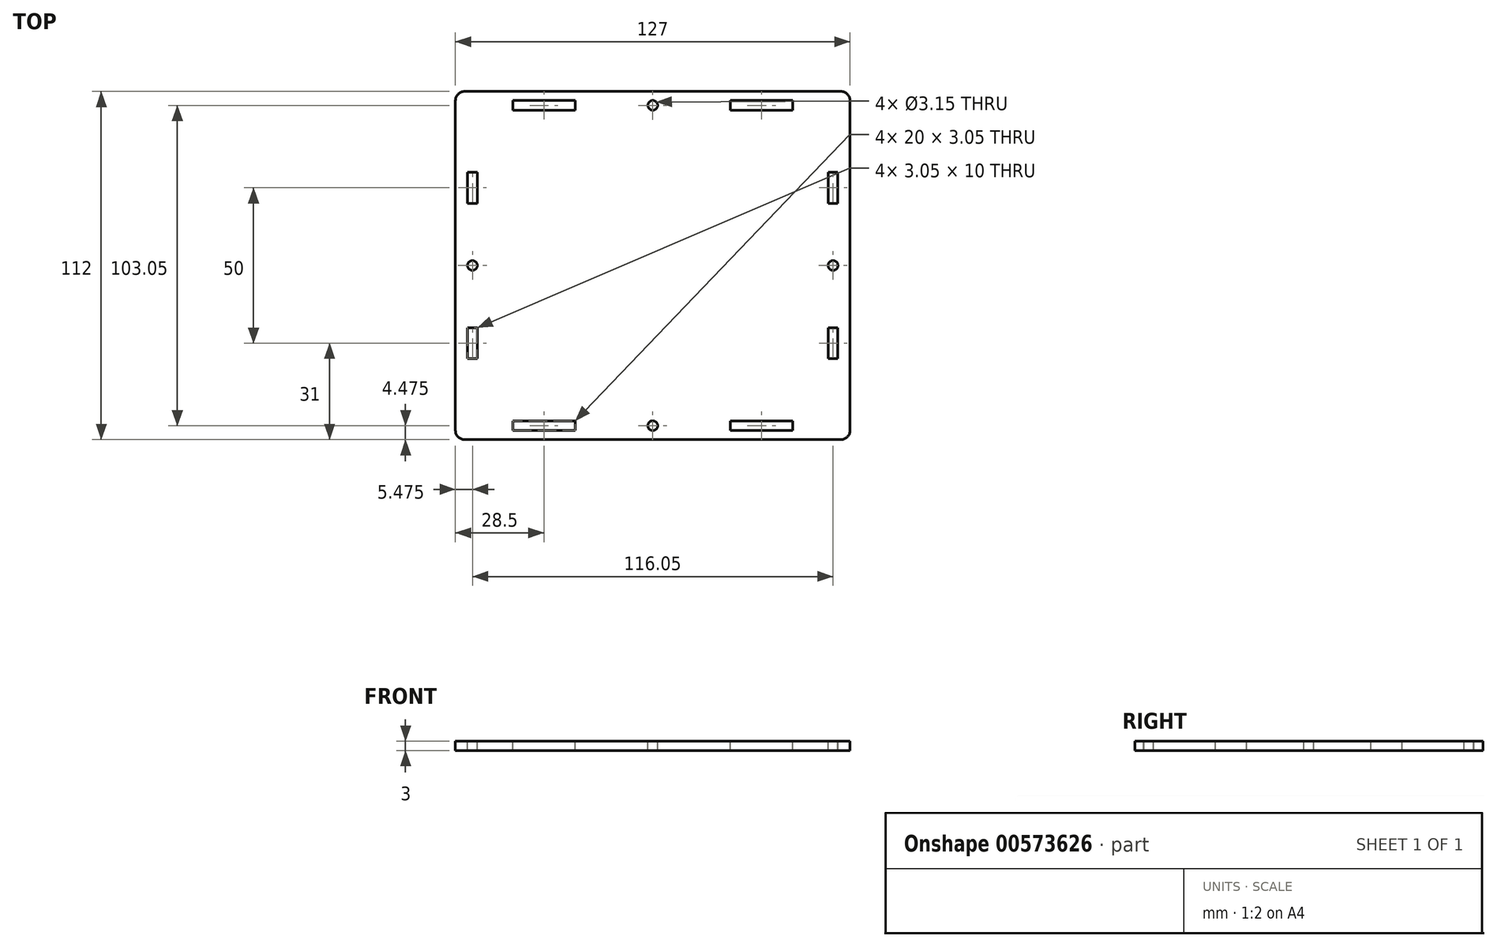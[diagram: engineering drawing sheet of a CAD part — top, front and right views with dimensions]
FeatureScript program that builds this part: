
annotation { "Feature Type Name" : "Feature", "Feature Type Description" : "" }
export const myFeature = defineFeature(function(context is Context, id is Id, definition is map)
    precondition{}
    {
        {
            var Q0;
            Q0=qCreatedBy(makeId("Top.planeOp"),FACE);
            var sketch = newSketch(context, id + "F0", { "sketchPlane" : qUnion([Q0])});
            skLineSegment(sketch, "E0.bottom", {"start": v(63.5, -56) * mm, "end": v(-63.5, -56) * mm});
            skLineSegment(sketch, "E0.top", {"start": v(63.5, 56) * mm, "end": v(-63.5, 56) * mm});
            skLineSegment(sketch, "E0.left", {"start": v(63.5, -56) * mm, "end": v(63.5, 56) * mm});
            skLineSegment(sketch, "E0.right", {"start": v(-63.5, -56) * mm, "end": v(-63.5, 56) * mm});
            skPoint(sketch, "E0.middle", {"position": v(0, 0) * mm});
            skSolve(sketch);
        }
        {
            var Q0;
            Q0 = qSketchRegion(id + "F0", true);
            extrude(context, id + "F1", {"entities" : qUnion([Q0]), "depth" : 3 * mm, "offsetDistance" : 25 * mm});
        }
        {
            var Q0;
            Q0=makeQuery(id+"F1.opExtrude","CAP_FACE",FACE,{"disambiguationData":[OSD([sQuery(id+"F0.wireOp",EDGE,"E0.bottom"),sQuery(id+"F0.wireOp",EDGE,"E0.top"),sQuery(id+"F0.wireOp",EDGE,"E0.left"),sQuery(id+"F0.wireOp",EDGE,"E0.right")])],"isStart":false});
            var sketch = newSketch(context, id + "F2", { "sketchPlane" : qUnion([Q0])});
            skLineSegment(sketch, "E1", {"start": v(0, 56) * mm, "end": v(0, -56) * mm, "construction": true});
            skLineSegment(sketch, "E2", {"start": v(-63.5, 0) * mm, "end": v(63.5, 0) * mm, "construction": true});
            skLineSegment(sketch, "E3.bottom", {"start": v(-56.5, 30) * mm, "end": v(-59.55, 30) * mm});
            skLineSegment(sketch, "E3.top", {"start": v(-56.5, 20) * mm, "end": v(-59.55, 20) * mm});
            skLineSegment(sketch, "E3.left", {"start": v(-56.5, 30) * mm, "end": v(-56.5, 20) * mm});
            skLineSegment(sketch, "E3.right", {"start": v(-59.55, 30) * mm, "end": v(-59.55, 20) * mm});
            skLineSegment(sketch, "E4.MirrorCS", {"start": v(-59.55, -30) * mm, "end": v(-59.55, -20) * mm});
            skLineSegment(sketch, "E5.MirrorCS", {"start": v(-56.5, -30) * mm, "end": v(-56.5, -20) * mm});
            skLineSegment(sketch, "E6.MirrorCS", {"start": v(-56.5, -30) * mm, "end": v(-59.55, -30) * mm});
            skLineSegment(sketch, "E7.MirrorCS", {"start": v(-56.5, -20) * mm, "end": v(-59.55, -20) * mm});
            skLineSegment(sketch, "E8", {"start": v(-58.02, 20) * mm, "end": v(-58.02, -20) * mm, "construction": true});
            skCircle(sketch, "E9", {"center": v(-58.02, 0) * mm, "radius": 1.57 * mm});
            skLineSegment(sketch, "E10.MirrorCS", {"start": v(56.5, -30) * mm, "end": v(59.55, -30) * mm});
            skLineSegment(sketch, "E11.MirrorCS", {"start": v(56.5, -20) * mm, "end": v(59.55, -20) * mm});
            skLineSegment(sketch, "E12.MirrorCS", {"start": v(56.5, 20) * mm, "end": v(59.55, 20) * mm});
            skLineSegment(sketch, "E13.MirrorCS", {"start": v(56.5, 30) * mm, "end": v(59.55, 30) * mm});
            skLineSegment(sketch, "E14.MirrorCS", {"start": v(56.5, -30) * mm, "end": v(56.5, -20) * mm});
            skLineSegment(sketch, "E15.MirrorCS", {"start": v(59.55, -30) * mm, "end": v(59.55, -20) * mm});
            skCircle(sketch, "E16.MirrorC", {"center": v(58.02, 0) * mm, "radius": 1.57 * mm});
            skLineSegment(sketch, "E17.MirrorCS", {"start": v(56.5, 30) * mm, "end": v(56.5, 20) * mm});
            skLineSegment(sketch, "E18.MirrorCS", {"start": v(59.55, 30) * mm, "end": v(59.55, 20) * mm});
            skLineSegment(sketch, "E19.bottom", {"start": v(-45, -50) * mm, "end": v(-25, -50) * mm});
            skLineSegment(sketch, "E19.top", {"start": v(-45, -53.05) * mm, "end": v(-25, -53.05) * mm});
            skLineSegment(sketch, "E19.left", {"start": v(-45, -50) * mm, "end": v(-45, -53.05) * mm});
            skLineSegment(sketch, "E19.right", {"start": v(-25, -50) * mm, "end": v(-25, -53.05) * mm});
            skLineSegment(sketch, "E20.MirrorCS", {"start": v(45, -50) * mm, "end": v(45, -53.05) * mm});
            skLineSegment(sketch, "E21.MirrorCS", {"start": v(25, -50) * mm, "end": v(25, -53.05) * mm});
            skLineSegment(sketch, "E22.MirrorCS", {"start": v(45, -50) * mm, "end": v(25, -50) * mm});
            skLineSegment(sketch, "E23.MirrorCS", {"start": v(45, -53.05) * mm, "end": v(25, -53.05) * mm});
            skLineSegment(sketch, "E24", {"start": v(-25, -51.52) * mm, "end": v(25, -51.52) * mm, "construction": true});
            skCircle(sketch, "E25", {"center": v(0, -51.52) * mm, "radius": 1.57 * mm});
            skLineSegment(sketch, "E26.MirrorCS", {"start": v(-25, 50) * mm, "end": v(-25, 53.05) * mm});
            skLineSegment(sketch, "E27.MirrorCS", {"start": v(25, 50) * mm, "end": v(25, 53.05) * mm});
            skLineSegment(sketch, "E28.MirrorCS", {"start": v(-45, 50) * mm, "end": v(-25, 50) * mm});
            skCircle(sketch, "E29.MirrorC", {"center": v(0, 51.52) * mm, "radius": 1.57 * mm});
            skLineSegment(sketch, "E30.MirrorCS", {"start": v(45, 50) * mm, "end": v(25, 50) * mm});
            skLineSegment(sketch, "E31.MirrorCS", {"start": v(-45, 50) * mm, "end": v(-45, 53.05) * mm});
            skLineSegment(sketch, "E32.MirrorCS", {"start": v(45, 53.05) * mm, "end": v(25, 53.05) * mm});
            skLineSegment(sketch, "E33.MirrorCS", {"start": v(-45, 53.05) * mm, "end": v(-25, 53.05) * mm});
            skLineSegment(sketch, "E34.MirrorCS", {"start": v(45, 50) * mm, "end": v(45, 53.05) * mm});
            skSolve(sketch);
        }
        {
            var Q0;
            Q0 = qSketchRegion(id + "F2", true);
            var Q1;
            Q1=makeQuery(id+"F1.opExtrude","CAP_FACE",FACE,{"disambiguationData":[OSD([sQuery(id+"F0.wireOp",EDGE,"E0.bottom"),sQuery(id+"F0.wireOp",EDGE,"E0.top"),sQuery(id+"F0.wireOp",EDGE,"E0.left"),sQuery(id+"F0.wireOp",EDGE,"E0.right")])],"isStart":true});
            extrude(context, id + "F3", {"entities" : qUnion([Q0]), "operationType" : NewBodyOperationType.REMOVE, "endBound" : BoundingType.UP_TO_SURFACE, "oppositeDirection" : true, "depth" : 25 * mm, "endBoundEntityFace" : qUnion([Q1]), "offsetDistance" : 25 * mm});
        }
        {
            var Q0;
            Q0=makeQuery(id+"F1.opExtrude","SWEPT_EDGE",EDGE,{"disambiguationData":[OSD([sQuery(id+"F0.wireOp",EDGE,"E0.bottom"),sQuery(id+"F0.wireOp",EDGE,"E0.left")])]});
            var Q1;
            Q1=makeQuery(id+"F1.opExtrude","SWEPT_EDGE",EDGE,{"disambiguationData":[OSD([sQuery(id+"F0.wireOp",EDGE,"E0.bottom"),sQuery(id+"F0.wireOp",EDGE,"E0.right")])]});
            var Q2;
            Q2=makeQuery(id+"F1.opExtrude","SWEPT_EDGE",EDGE,{"disambiguationData":[OSD([sQuery(id+"F0.wireOp",EDGE,"E0.top"),sQuery(id+"F0.wireOp",EDGE,"E0.right")])]});
            var Q3;
            Q3=makeQuery(id+"F1.opExtrude","SWEPT_EDGE",EDGE,{"disambiguationData":[OSD([sQuery(id+"F0.wireOp",EDGE,"E0.top"),sQuery(id+"F0.wireOp",EDGE,"E0.left")])]});
            fillet(context, id + "F4", {"entities" : qUnion([Q0, Q1, Q2, Q3]), "radius" : 3 * mm, "tangentPropagation" : true, "allowEdgeOverflow" : false});
        }
    });
